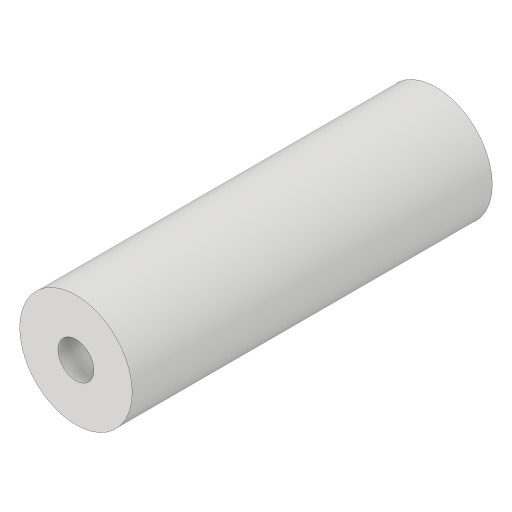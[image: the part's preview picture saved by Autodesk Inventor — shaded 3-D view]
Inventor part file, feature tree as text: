
AUTODESK INVENTOR PART (.ipt)
format: ipt  version: 2023.2 (Build 272271000, 271)  size: 108,544 bytes
history: native  units: mm
features: other x1, extrude x1, sketch x1
ambient origin geometry x8: Origin, YZ Plane, XZ Plane, XY Plane, X Axis, Y Axis, Z Axis, Center Point
bodies: Body1 (feature_tree)
feature tree (3):
  other  "솔리드1"
  extrude  "돌출1"  Depth=3.2mm
  sketch  "스케치1"
